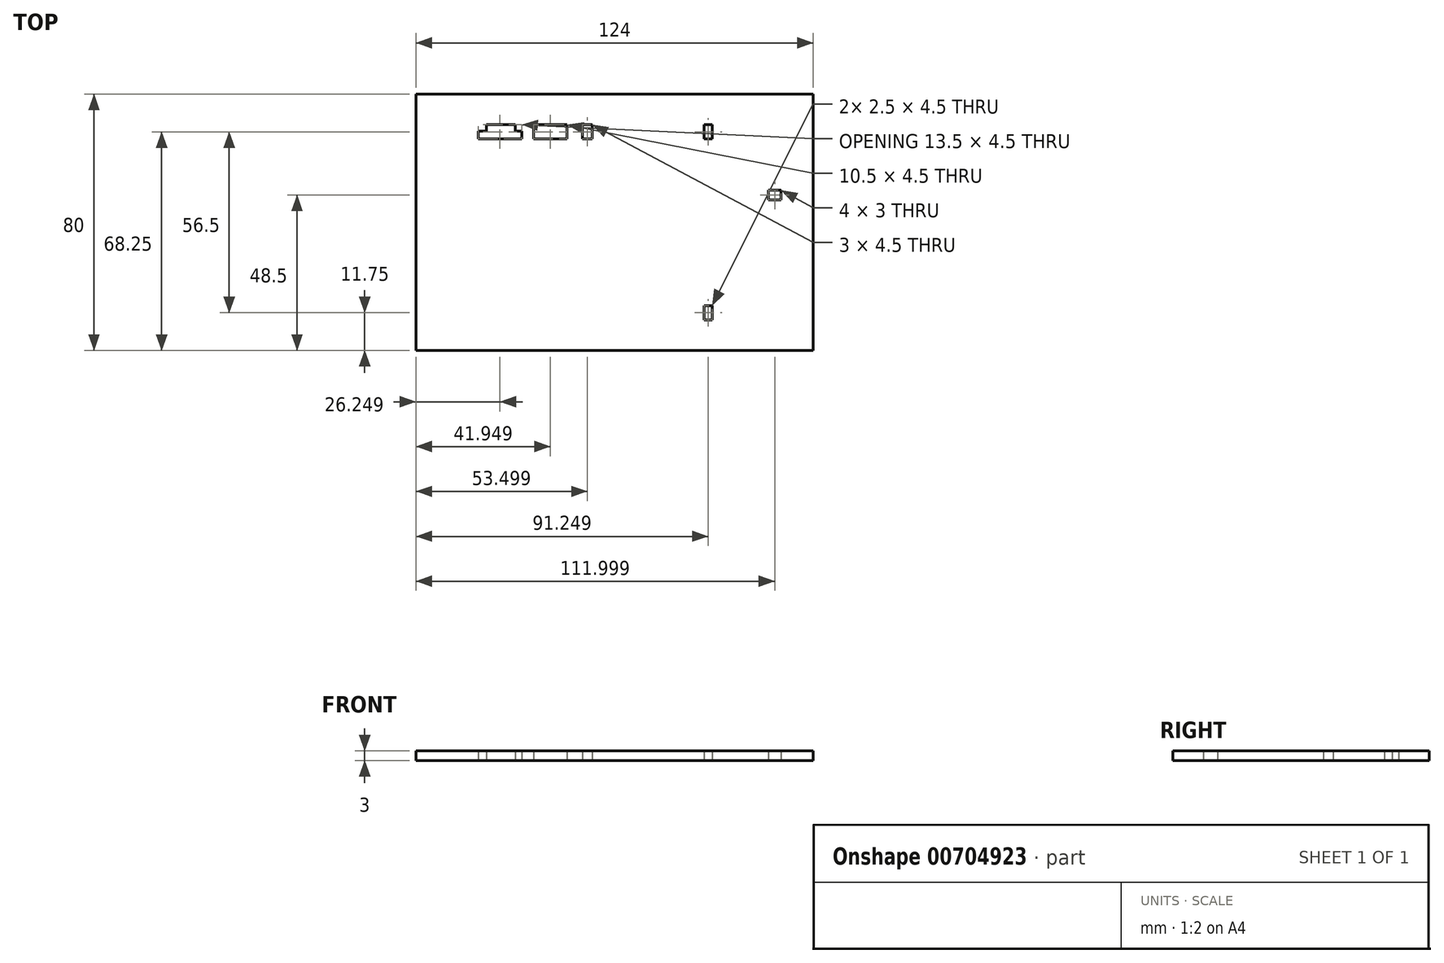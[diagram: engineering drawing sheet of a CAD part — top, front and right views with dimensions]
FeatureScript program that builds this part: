
annotation { "Feature Type Name" : "Feature", "Feature Type Description" : "" }
export const myFeature = defineFeature(function(context is Context, id is Id, definition is map)
    precondition{}
    {
        {
            var Q0;
            Q0=qCreatedBy(makeId("Top.planeOp"),FACE);
            var sketch = newSketch(context, id + "F0", { "sketchPlane" : qUnion([Q0])});
            skLineSegment(sketch, "E0.bottom", {"start": v(-68.04, 70) * mm, "end": v(55.96, 70) * mm});
            skLineSegment(sketch, "E0.top", {"start": v(-68.04, -10) * mm, "end": v(55.96, -10) * mm});
            skLineSegment(sketch, "E0.left", {"start": v(-68.04, 70) * mm, "end": v(-68.04, -10) * mm});
            skLineSegment(sketch, "E0.right", {"start": v(55.96, 70) * mm, "end": v(55.96, -10) * mm});
            skLineSegment(sketch, "E1.MirrorCS", {"start": v(-16.04, 56) * mm, "end": v(-13.04, 56) * mm});
            skLineSegment(sketch, "E2.MirrorCS", {"start": v(-16.04, 60.5) * mm, "end": v(-16.04, 56) * mm});
            skLineSegment(sketch, "E3.MirrorCS", {"start": v(-35.04, 56) * mm, "end": v(-35.04, 58.5) * mm});
            skLineSegment(sketch, "E4.MirrorCS", {"start": v(-35.04, 58.5) * mm, "end": v(-37.04, 58.5) * mm});
            skLineSegment(sketch, "E5.MirrorCS", {"start": v(-46.04, 60.5) * mm, "end": v(-46.04, 58.5) * mm});
            skLineSegment(sketch, "E6", {"start": v(-20.84, 56) * mm, "end": v(-31.34, 56) * mm});
            skLineSegment(sketch, "E7", {"start": v(-31.34, 56) * mm, "end": v(-31.34, 60.5) * mm});
            skLineSegment(sketch, "E8", {"start": v(-46.04, 58.5) * mm, "end": v(-48.54, 58.5) * mm});
            skLineSegment(sketch, "E9", {"start": v(-35.04, 56) * mm, "end": v(-48.54, 56) * mm});
            skLineSegment(sketch, "E10", {"start": v(-48.54, 56) * mm, "end": v(-48.54, 58.5) * mm});
            skLineSegment(sketch, "E11", {"start": v(-46.04, 60.5) * mm, "end": v(-37.04, 60.5) * mm});
            skLineSegment(sketch, "E12", {"start": v(-37.04, 60.5) * mm, "end": v(-37.04, 58.5) * mm});
            skLineSegment(sketch, "E13", {"start": v(-31.34, 60.5) * mm, "end": v(-20.84, 60.5) * mm});
            skLineSegment(sketch, "E14", {"start": v(-20.84, 60.5) * mm, "end": v(-20.84, 56) * mm});
            skLineSegment(sketch, "E15", {"start": v(-13.04, 56) * mm, "end": v(-13.04, 60.5) * mm});
            skLineSegment(sketch, "E16", {"start": v(-13.04, 60.5) * mm, "end": v(-16.04, 60.5) * mm});
            skLineSegment(sketch, "E17", {"start": v(21.96, 56) * mm, "end": v(21.96, 60.5) * mm});
            skLineSegment(sketch, "E18", {"start": v(21.96, 60.5) * mm, "end": v(24.46, 60.5) * mm});
            skLineSegment(sketch, "E19", {"start": v(24.46, 60.5) * mm, "end": v(24.46, 56) * mm});
            skLineSegment(sketch, "E20", {"start": v(24.46, 56) * mm, "end": v(21.96, 56) * mm});
            skLineSegment(sketch, "E21", {"start": v(45.96, 40) * mm, "end": v(41.96, 40) * mm});
            skLineSegment(sketch, "E22", {"start": v(41.96, 40) * mm, "end": v(41.96, 37) * mm});
            skLineSegment(sketch, "E23", {"start": v(41.96, 37) * mm, "end": v(45.96, 37) * mm});
            skLineSegment(sketch, "E24", {"start": v(45.96, 37) * mm, "end": v(45.96, 40) * mm});
            skLineSegment(sketch, "E25.MirrorCS", {"start": v(21.96, 4) * mm, "end": v(21.96, -0.5) * mm});
            skLineSegment(sketch, "E26.MirrorCS", {"start": v(21.96, -0.5) * mm, "end": v(24.46, -0.5) * mm});
            skLineSegment(sketch, "E27.MirrorCS", {"start": v(24.46, 4) * mm, "end": v(21.96, 4) * mm});
            skLineSegment(sketch, "E28.MirrorCS", {"start": v(24.46, -0.5) * mm, "end": v(24.46, 4) * mm});
            skSolve(sketch);
        }
        {
            var Q0;
            Q0=makeQuery(id+"F0.imprint","IMPRINT",FACE,{"disambiguationData":[TD([[makeQuery(id+"F0.imprint","IMPRINT",EDGE,{"derivedFrom":sQuery(id+"F0.wireOp",EDGE,"UEqrDGLH-FFpF-oJ1Q-Opp3-dnx0jUD92dck")}),1.0]])]});
            var Q1;
            Q1=makeQuery(id+"F0.imprint","IMPRINT",FACE,{"disambiguationData":[TD([[makeQuery(id+"F0.imprint","IMPRINT",EDGE,{"derivedFrom":sQuery(id+"F0.wireOp",EDGE,"E0.bottom")}),-1.0]])]});
            extrude(context, id + "F1", {"entities" : qUnion([Q0, Q1]), "depth" : 3 * mm, "offsetDistance" : 25 * mm});
        }
    });
